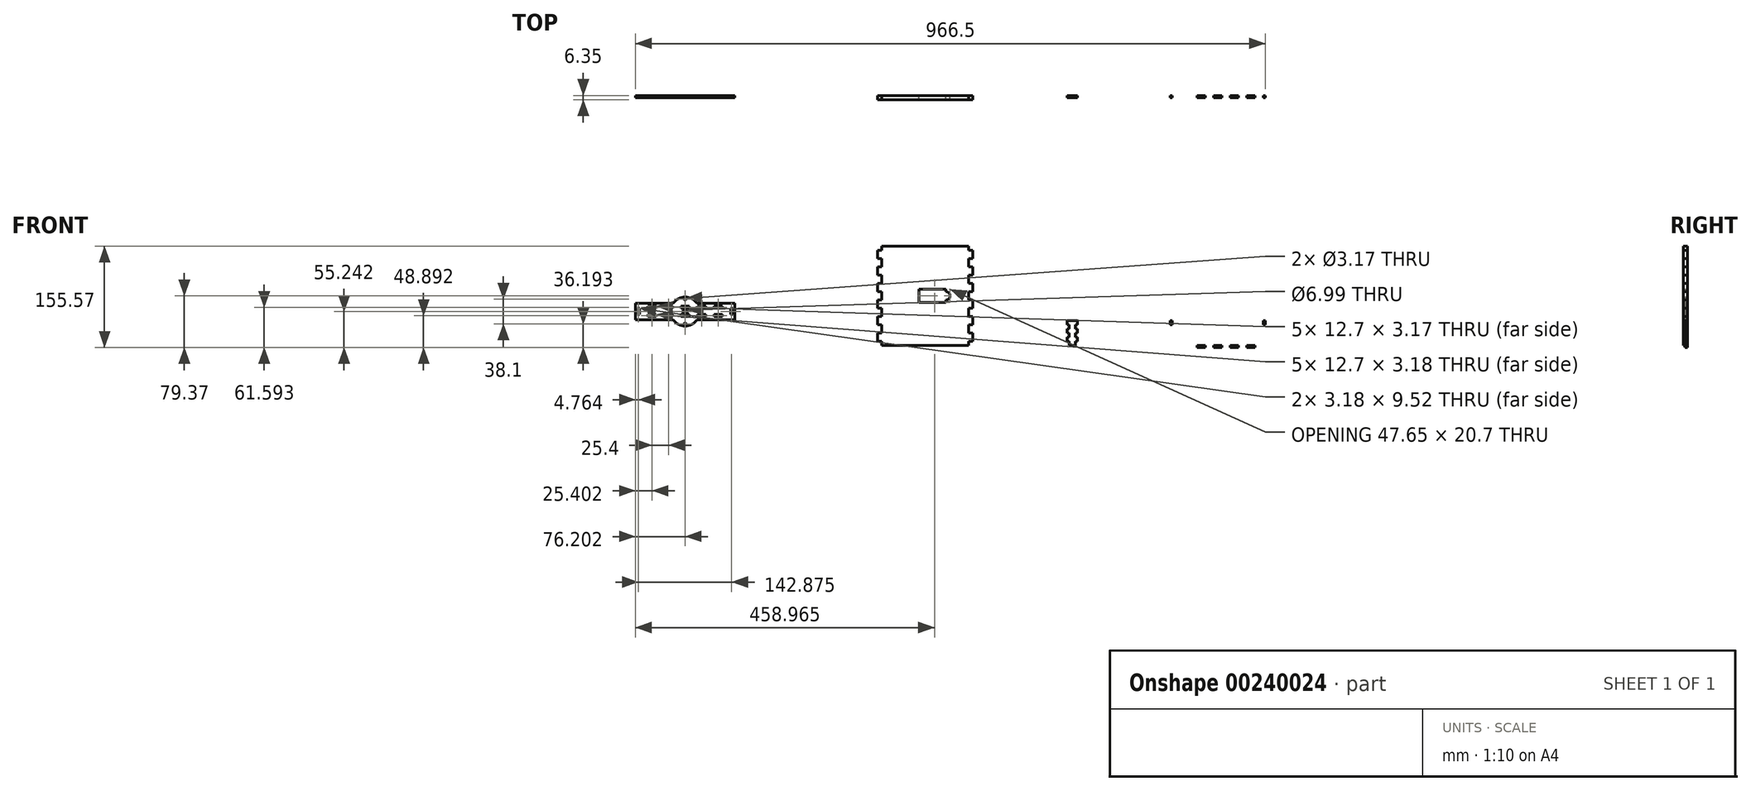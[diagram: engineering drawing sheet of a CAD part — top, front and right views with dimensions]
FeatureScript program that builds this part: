
annotation { "Feature Type Name" : "Feature", "Feature Type Description" : "" }
export const myFeature = defineFeature(function(context is Context, id is Id, definition is map)
    precondition{}
    {
        {
            var Q0;
            Q0=qCreatedBy(makeId("Front.planeOp"),FACE);
            var sketch = newSketch(context, id + "F0", { "sketchPlane" : qUnion([Q0])});
            skLineSegment(sketch, "E0.bottom", {"start": v(0, 0) * mm, "end": v(146.05, 0) * mm});
            skLineSegment(sketch, "E0.top", {"start": v(0, 38.1) * mm, "end": v(146.05, 38.1) * mm});
            skLineSegment(sketch, "E0.left", {"start": v(0, 0) * mm, "end": v(0, 38.1) * mm});
            skLineSegment(sketch, "E0.right", {"start": v(146.05, 0) * mm, "end": v(146.05, 38.1) * mm});
            skLineSegment(sketch, "E1.bottom", {"start": v(0, 38.1) * mm, "end": v(3.17, 38.1) * mm});
            skLineSegment(sketch, "E1.top", {"start": v(0, 31.75) * mm, "end": v(3.17, 31.75) * mm});
            skLineSegment(sketch, "E1.left", {"start": v(0, 38.1) * mm, "end": v(0, 31.75) * mm});
            skLineSegment(sketch, "E1.right", {"start": v(3.17, 38.1) * mm, "end": v(3.17, 31.75) * mm});
            skLineSegment(sketch, "E2.0.1.0", {"start": v(0, 19.05) * mm, "end": v(3.17, 19.05) * mm});
            skLineSegment(sketch, "E2.0.1.1", {"start": v(3.17, 25.4) * mm, "end": v(3.17, 19.05) * mm});
            skLineSegment(sketch, "E2.0.1.2", {"start": v(0, 25.4) * mm, "end": v(3.17, 25.4) * mm});
            skLineSegment(sketch, "E2.0.1.3", {"start": v(0, 25.4) * mm, "end": v(0, 19.05) * mm});
            skLineSegment(sketch, "E2.0.2.0", {"start": v(0, 6.35) * mm, "end": v(3.17, 6.35) * mm});
            skLineSegment(sketch, "E2.0.2.1", {"start": v(3.17, 12.7) * mm, "end": v(3.17, 6.35) * mm});
            skLineSegment(sketch, "E2.0.2.2", {"start": v(0, 12.7) * mm, "end": v(3.17, 12.7) * mm});
            skLineSegment(sketch, "E2.0.2.3", {"start": v(0, 12.7) * mm, "end": v(0, 6.35) * mm});
            skLineSegment(sketch, "E2.direction1", {"start": v(0, 25.4) * mm, "end": v(25.4, 25.4) * mm, "construction": true});
            skLineSegment(sketch, "E2.direction2", {"start": v(0, 25.4) * mm, "end": v(0, 12.7) * mm, "construction": true});
            skLineSegment(sketch, "E3.bottom", {"start": v(15.88, 0) * mm, "end": v(28.58, 0) * mm});
            skLineSegment(sketch, "E3.top", {"start": v(15.88, -3.18) * mm, "end": v(28.58, -3.18) * mm});
            skLineSegment(sketch, "E3.left", {"start": v(15.88, 0) * mm, "end": v(15.88, -3.18) * mm});
            skLineSegment(sketch, "E3.right", {"start": v(28.58, 0) * mm, "end": v(28.58, -3.18) * mm});
            skLineSegment(sketch, "E4.1.0.0", {"start": v(41.27, -3.18) * mm, "end": v(53.97, -3.18) * mm});
            skLineSegment(sketch, "E4.1.0.1", {"start": v(53.97, 0) * mm, "end": v(53.97, -3.18) * mm});
            skLineSegment(sketch, "E4.1.0.2", {"start": v(41.27, 0) * mm, "end": v(41.27, -3.18) * mm});
            skLineSegment(sketch, "E4.1.0.3", {"start": v(41.27, 0) * mm, "end": v(53.97, 0) * mm});
            skLineSegment(sketch, "E4.2.0.0", {"start": v(66.67, -3.18) * mm, "end": v(79.37, -3.18) * mm});
            skLineSegment(sketch, "E4.2.0.1", {"start": v(79.37, 0) * mm, "end": v(79.37, -3.18) * mm});
            skLineSegment(sketch, "E4.2.0.2", {"start": v(66.67, 0) * mm, "end": v(66.67, -3.18) * mm});
            skLineSegment(sketch, "E4.2.0.3", {"start": v(66.67, 0) * mm, "end": v(79.37, 0) * mm});
            skLineSegment(sketch, "E4.3.0.0", {"start": v(92.07, -3.18) * mm, "end": v(104.77, -3.18) * mm});
            skLineSegment(sketch, "E4.3.0.1", {"start": v(104.77, 0) * mm, "end": v(104.77, -3.18) * mm});
            skLineSegment(sketch, "E4.3.0.2", {"start": v(92.07, 0) * mm, "end": v(92.07, -3.18) * mm});
            skLineSegment(sketch, "E4.3.0.3", {"start": v(92.07, 0) * mm, "end": v(104.77, 0) * mm});
            skLineSegment(sketch, "E4.4.0.0", {"start": v(117.47, -3.18) * mm, "end": v(130.17, -3.18) * mm});
            skLineSegment(sketch, "E4.4.0.1", {"start": v(130.17, 0) * mm, "end": v(130.17, -3.18) * mm});
            skLineSegment(sketch, "E4.4.0.2", {"start": v(117.47, 0) * mm, "end": v(117.47, -3.18) * mm});
            skLineSegment(sketch, "E4.4.0.3", {"start": v(117.47, 0) * mm, "end": v(130.17, 0) * mm});
            skLineSegment(sketch, "E4.direction1", {"start": v(3.18, -3.18) * mm, "end": v(28.58, -3.18) * mm, "construction": true});
            skLineSegment(sketch, "E5", {"start": v(73.03, 38.1) * mm, "end": v(73.03, 0) * mm, "construction": true});
            skLineSegment(sketch, "E6.MirrorCS", {"start": v(146.05, 12.7) * mm, "end": v(142.88, 12.7) * mm});
            skLineSegment(sketch, "E7.MirrorCS", {"start": v(146.05, 31.75) * mm, "end": v(142.88, 31.75) * mm});
            skLineSegment(sketch, "E8.MirrorCS", {"start": v(146.05, 19.05) * mm, "end": v(142.88, 19.05) * mm});
            skLineSegment(sketch, "E9.MirrorCS", {"start": v(146.05, 25.4) * mm, "end": v(142.88, 25.4) * mm});
            skLineSegment(sketch, "E10.MirrorCS", {"start": v(146.05, 6.35) * mm, "end": v(142.88, 6.35) * mm});
            skLineSegment(sketch, "E11.MirrorCS", {"start": v(142.88, 12.7) * mm, "end": v(142.88, 6.35) * mm});
            skLineSegment(sketch, "E12.MirrorCS", {"start": v(142.88, 38.1) * mm, "end": v(142.88, 31.75) * mm});
            skLineSegment(sketch, "E13.MirrorCS", {"start": v(142.88, 25.4) * mm, "end": v(142.88, 19.05) * mm});
            skLineSegment(sketch, "E14.MirrorCS", {"start": v(146.05, 25.4) * mm, "end": v(120.65, 25.4) * mm, "construction": true});
            skLineSegment(sketch, "E15.MirrorCS", {"start": v(146.05, 38.1) * mm, "end": v(142.88, 38.1) * mm});
            skLineSegment(sketch, "E16.MirrorCS", {"start": v(146.05, 38.1) * mm, "end": v(146.05, 31.75) * mm});
            skLineSegment(sketch, "E17.MirrorCS", {"start": v(146.05, 25.4) * mm, "end": v(146.05, 12.7) * mm, "construction": true});
            skSolve(sketch);
        }
        {
            var Q0;
            Q0=makeQuery(id+"F0.imprint","IMPRINT",FACE,{"disambiguationData":[TD([[makeQuery(id+"F0.imprint","IMPRINT",EDGE,{"derivedFrom":sQuery(id+"F0.wireOp",EDGE,"E0.top")}),-1.0]])]});
            var Q1;
            Q1=makeQuery(id+"F0.imprint","IMPRINT",FACE,{"disambiguationData":[TD([[makeQuery(id+"F0.imprint","IMPRINT",EDGE,{"derivedFrom":sQuery(id+"F0.wireOp",EDGE,"E3.bottom")}),-1.0]])]});
            var Q2;
            Q2=makeQuery(id+"F0.imprint","IMPRINT",FACE,{"disambiguationData":[TD([[makeQuery(id+"F0.imprint","IMPRINT",EDGE,{"derivedFrom":sQuery(id+"F0.wireOp",EDGE,"E4.1.0.0")}),1.0]])]});
            var Q3;
            Q3=makeQuery(id+"F0.imprint","IMPRINT",FACE,{"disambiguationData":[TD([[makeQuery(id+"F0.imprint","IMPRINT",EDGE,{"derivedFrom":sQuery(id+"F0.wireOp",EDGE,"E4.2.0.0")}),1.0]])]});
            var Q4;
            Q4=makeQuery(id+"F0.imprint","IMPRINT",FACE,{"disambiguationData":[TD([[makeQuery(id+"F0.imprint","IMPRINT",EDGE,{"derivedFrom":sQuery(id+"F0.wireOp",EDGE,"E4.3.0.0")}),1.0]])]});
            var Q5;
            Q5=makeQuery(id+"F0.imprint","IMPRINT",FACE,{"disambiguationData":[TD([[makeQuery(id+"F0.imprint","IMPRINT",EDGE,{"derivedFrom":sQuery(id+"F0.wireOp",EDGE,"E4.4.0.0")}),1.0]])]});
            extrude(context, id + "F1", {"entities" : qUnion([Q0, Q1, Q2, Q3, Q4, Q5]), "depth" : 3.17 * mm});
        }
        {
            var Q0;
            Q0=qCreatedBy(makeId("Front.planeOp"),FACE);
            var sketch = newSketch(context, id + "F2", { "sketchPlane" : qUnion([Q0])});
            skLineSegment(sketch, "E18.bottom", {"start": v(-145.64, 0) * mm, "end": v(-155.16, 0) * mm});
            skLineSegment(sketch, "E18.top", {"start": v(-145.64, 38.1) * mm, "end": v(-155.16, 38.1) * mm});
            skLineSegment(sketch, "E18.left", {"start": v(-145.64, 0) * mm, "end": v(-145.64, 38.1) * mm});
            skLineSegment(sketch, "E18.right", {"start": v(-155.16, 0) * mm, "end": v(-155.16, 38.1) * mm});
            skLineSegment(sketch, "E19.bottom", {"start": v(-145.64, 38.1) * mm, "end": v(-142.46, 38.1) * mm});
            skLineSegment(sketch, "E19.top", {"start": v(-145.64, 31.75) * mm, "end": v(-142.46, 31.75) * mm});
            skLineSegment(sketch, "E19.left", {"start": v(-145.64, 38.1) * mm, "end": v(-145.64, 31.75) * mm});
            skLineSegment(sketch, "E19.right", {"start": v(-142.46, 38.1) * mm, "end": v(-142.46, 31.75) * mm});
            skLineSegment(sketch, "E20.0.1.0", {"start": v(-142.46, 25.4) * mm, "end": v(-142.46, 19.05) * mm});
            skLineSegment(sketch, "E20.0.1.1", {"start": v(-145.64, 25.4) * mm, "end": v(-142.46, 25.4) * mm});
            skLineSegment(sketch, "E20.0.1.2", {"start": v(-145.64, 19.05) * mm, "end": v(-142.46, 19.05) * mm});
            skLineSegment(sketch, "E20.0.1.3", {"start": v(-155.16, -12.7) * mm, "end": v(-155.16, 25.4) * mm});
            skLineSegment(sketch, "E20.0.2.0", {"start": v(-142.46, 12.7) * mm, "end": v(-142.46, 6.35) * mm});
            skLineSegment(sketch, "E20.0.2.1", {"start": v(-145.64, 12.7) * mm, "end": v(-142.46, 12.7) * mm});
            skLineSegment(sketch, "E20.0.2.2", {"start": v(-145.64, 6.35) * mm, "end": v(-142.46, 6.35) * mm});
            skLineSegment(sketch, "E20.0.2.3", {"start": v(-155.16, -25.4) * mm, "end": v(-155.16, 12.7) * mm});
            skLineSegment(sketch, "E20.direction1", {"start": v(-145.64, 31.75) * mm, "end": v(-122.14, 31.75) * mm, "construction": true});
            skLineSegment(sketch, "E20.direction2", {"start": v(-145.64, 31.75) * mm, "end": v(-145.64, 19.05) * mm, "construction": true});
            skLineSegment(sketch, "E21", {"start": v(-150.4, 38.1) * mm, "end": v(-150.4, 0) * mm, "construction": true});
            skLineSegment(sketch, "E22.MirrorCS", {"start": v(-155.16, 25.4) * mm, "end": v(-158.34, 25.4) * mm});
            skLineSegment(sketch, "E23.MirrorCS", {"start": v(-155.16, 19.05) * mm, "end": v(-158.34, 19.05) * mm});
            skLineSegment(sketch, "E24.MirrorCS", {"start": v(-155.16, 31.75) * mm, "end": v(-158.34, 31.75) * mm});
            skLineSegment(sketch, "E25.MirrorCS", {"start": v(-155.16, 38.1) * mm, "end": v(-158.34, 38.1) * mm});
            skLineSegment(sketch, "E26.MirrorCS", {"start": v(-155.16, 12.7) * mm, "end": v(-158.34, 12.7) * mm});
            skLineSegment(sketch, "E27.MirrorCS", {"start": v(-155.16, 6.35) * mm, "end": v(-158.34, 6.35) * mm});
            skLineSegment(sketch, "E28.MirrorCS", {"start": v(-158.34, 38.1) * mm, "end": v(-158.34, 31.75) * mm});
            skLineSegment(sketch, "E29.MirrorCS", {"start": v(-158.34, 25.4) * mm, "end": v(-158.34, 19.05) * mm});
            skLineSegment(sketch, "E30.MirrorCS", {"start": v(-158.34, 12.7) * mm, "end": v(-158.34, 6.35) * mm});
            skLineSegment(sketch, "E31.MirrorCS", {"start": v(-155.16, 31.75) * mm, "end": v(-178.66, 31.75) * mm, "construction": true});
            skLineSegment(sketch, "E32.bottom", {"start": v(-155.16, 0) * mm, "end": v(-145.64, 0) * mm});
            skLineSegment(sketch, "E32.top", {"start": v(-155.16, -3.18) * mm, "end": v(-145.64, -3.18) * mm});
            skLineSegment(sketch, "E32.left", {"start": v(-155.16, 0) * mm, "end": v(-155.16, -3.18) * mm});
            skLineSegment(sketch, "E32.right", {"start": v(-145.64, 0) * mm, "end": v(-145.64, -3.18) * mm});
            skSolve(sketch);
        }
        {
            var Q0;
            {var subQ7=sQuery(id+"F2.wireOp",EDGE,"E18.top");Q0=makeQuery(id+"F2.imprint","IMPRINT",FACE,{"disambiguationData":[TD([[makeQuery(id+"F2.imprint","IMPRINT",EDGE,{"derivedFrom":subQ7}),1.0]])]});}
            var Q1;
            {var subQ0=sQuery(id+"F2.wireOp",EDGE,"E22.MirrorCS");Q1=makeQuery(id+"F2.imprint","IMPRINT",FACE,{"disambiguationData":[TD([[makeQuery(id+"F2.imprint","IMPRINT",EDGE,{"derivedFrom":subQ0}),1.0]])]});}
            var Q2;
            {var subQ0=sQuery(id+"F2.wireOp",EDGE,"E26.MirrorCS");Q2=makeQuery(id+"F2.imprint","IMPRINT",FACE,{"disambiguationData":[TD([[makeQuery(id+"F2.imprint","IMPRINT",EDGE,{"derivedFrom":subQ0}),1.0]])]});}
            var Q3;
            Q3=makeQuery(id+"F2.imprint","IMPRINT",FACE,{"disambiguationData":[TD([[makeQuery(id+"F2.imprint","IMPRINT",EDGE,{"derivedFrom":sQuery(id+"F2.wireOp",EDGE,"E20.0.2.0")}),-1.0]])]});
            var Q4;
            Q4=makeQuery(id+"F2.imprint","IMPRINT",FACE,{"disambiguationData":[TD([[makeQuery(id+"F2.imprint","IMPRINT",EDGE,{"derivedFrom":sQuery(id+"F2.wireOp",EDGE,"E20.0.1.0")}),-1.0]])]});
            var Q5;
            Q5=makeQuery(id+"F2.imprint","IMPRINT",FACE,{"disambiguationData":[TD([[makeQuery(id+"F2.imprint","IMPRINT",EDGE,{"derivedFrom":sQuery(id+"F2.wireOp",EDGE,"E19.bottom")}),-1.0]])]});
            var Q6;
            {var subQ2=sQuery(id+"F2.wireOp",EDGE,"E24.MirrorCS");Q6=makeQuery(id+"F2.imprint","IMPRINT",FACE,{"disambiguationData":[TD([[makeQuery(id+"F2.imprint","IMPRINT",EDGE,{"derivedFrom":subQ2}),-1.0]])]});}
            var Q7;
            Q7=makeQuery(id+"F2.imprint","IMPRINT",FACE,{"disambiguationData":[TD([[makeQuery(id+"F2.imprint","IMPRINT",EDGE,{"derivedFrom":sQuery(id+"F2.wireOp",EDGE,"E32.bottom")}),-1.0]])]});
            extrude(context, id + "F3", {"entities" : qUnion([Q0, Q1, Q2, Q3, Q4, Q5, Q6, Q7]), "depth" : 3.17 * mm});
        }
        {
            var Q0;
            Q0=qCreatedBy(makeId("Front.planeOp"),FACE);
            var sketch = newSketch(context, id + "F4", { "sketchPlane" : qUnion([Q0])});
            skLineSegment(sketch, "E33.bottom", {"start": v(-309.1, 0) * mm, "end": v(-442.46, 0) * mm});
            skLineSegment(sketch, "E33.top", {"start": v(-309.1, 152.4) * mm, "end": v(-442.46, 152.4) * mm});
            skLineSegment(sketch, "E33.left", {"start": v(-309.1, 0) * mm, "end": v(-309.1, 152.4) * mm});
            skLineSegment(sketch, "E33.right", {"start": v(-442.46, 0) * mm, "end": v(-442.46, 152.4) * mm});
            skLineSegment(sketch, "E34.bottom", {"start": v(-309.1, 146.05) * mm, "end": v(-302.76, 146.05) * mm});
            skLineSegment(sketch, "E34.top", {"start": v(-309.1, 133.35) * mm, "end": v(-302.76, 133.35) * mm});
            skLineSegment(sketch, "E34.left", {"start": v(-309.1, 146.05) * mm, "end": v(-309.1, 133.35) * mm});
            skLineSegment(sketch, "E34.right", {"start": v(-302.76, 146.05) * mm, "end": v(-302.76, 133.35) * mm});
            skLineSegment(sketch, "E35.0.1.0", {"start": v(-309.1, 107.95) * mm, "end": v(-302.76, 107.95) * mm});
            skLineSegment(sketch, "E35.0.1.1", {"start": v(-309.1, 120.65) * mm, "end": v(-302.76, 120.65) * mm});
            skLineSegment(sketch, "E35.0.1.2", {"start": v(-302.76, 120.65) * mm, "end": v(-302.76, 107.95) * mm});
            skLineSegment(sketch, "E35.0.2.0", {"start": v(-309.1, 82.55) * mm, "end": v(-302.76, 82.55) * mm});
            skLineSegment(sketch, "E35.0.2.1", {"start": v(-309.1, 95.25) * mm, "end": v(-302.76, 95.25) * mm});
            skLineSegment(sketch, "E35.0.2.2", {"start": v(-302.76, 95.25) * mm, "end": v(-302.76, 82.55) * mm});
            skLineSegment(sketch, "E35.0.3.0", {"start": v(-309.1, 57.15) * mm, "end": v(-302.76, 57.15) * mm});
            skLineSegment(sketch, "E35.0.3.1", {"start": v(-309.1, 69.85) * mm, "end": v(-302.76, 69.85) * mm});
            skLineSegment(sketch, "E35.0.3.2", {"start": v(-302.76, 69.85) * mm, "end": v(-302.76, 57.15) * mm});
            skLineSegment(sketch, "E35.0.4.0", {"start": v(-309.1, 31.75) * mm, "end": v(-302.76, 31.75) * mm});
            skLineSegment(sketch, "E35.0.4.1", {"start": v(-309.1, 44.45) * mm, "end": v(-302.76, 44.45) * mm});
            skLineSegment(sketch, "E35.0.4.2", {"start": v(-302.76, 44.45) * mm, "end": v(-302.76, 31.75) * mm});
            skLineSegment(sketch, "E35.0.5.0", {"start": v(-309.1, 6.35) * mm, "end": v(-302.76, 6.35) * mm});
            skLineSegment(sketch, "E35.0.5.1", {"start": v(-309.1, 19.05) * mm, "end": v(-302.76, 19.05) * mm});
            skLineSegment(sketch, "E35.0.5.2", {"start": v(-302.76, 19.05) * mm, "end": v(-302.76, 6.35) * mm});
            skLineSegment(sketch, "E35.direction1", {"start": v(-309.1, 133.35) * mm, "end": v(-283.7, 133.35) * mm, "construction": true});
            skLineSegment(sketch, "E35.direction2", {"start": v(-309.1, 133.35) * mm, "end": v(-309.1, 107.95) * mm, "construction": true});
            skLineSegment(sketch, "E36", {"start": v(-375.78, 152.4) * mm, "end": v(-375.78, 0) * mm, "construction": true});
            skLineSegment(sketch, "E37.MirrorCS", {"start": v(-442.46, 31.75) * mm, "end": v(-448.8, 31.75) * mm});
            skLineSegment(sketch, "E38.MirrorCS", {"start": v(-442.46, 57.15) * mm, "end": v(-448.8, 57.15) * mm});
            skLineSegment(sketch, "E39.MirrorCS", {"start": v(-442.46, 69.85) * mm, "end": v(-448.8, 69.85) * mm});
            skLineSegment(sketch, "E40.MirrorCS", {"start": v(-442.46, 146.05) * mm, "end": v(-448.8, 146.05) * mm});
            skLineSegment(sketch, "E41.MirrorCS", {"start": v(-442.46, 133.35) * mm, "end": v(-448.8, 133.35) * mm});
            skLineSegment(sketch, "E42.MirrorCS", {"start": v(-442.46, 107.95) * mm, "end": v(-448.8, 107.95) * mm});
            skLineSegment(sketch, "E43.MirrorCS", {"start": v(-442.46, 120.65) * mm, "end": v(-448.8, 120.65) * mm});
            skLineSegment(sketch, "E44.MirrorCS", {"start": v(-442.46, 6.35) * mm, "end": v(-448.8, 6.35) * mm});
            skLineSegment(sketch, "E45.MirrorCS", {"start": v(-442.46, 19.05) * mm, "end": v(-448.8, 19.05) * mm});
            skLineSegment(sketch, "E46.MirrorCS", {"start": v(-442.46, 82.55) * mm, "end": v(-448.8, 82.55) * mm});
            skLineSegment(sketch, "E47.MirrorCS", {"start": v(-442.46, 44.45) * mm, "end": v(-448.8, 44.45) * mm});
            skLineSegment(sketch, "E48.MirrorCS", {"start": v(-442.46, 95.25) * mm, "end": v(-448.8, 95.25) * mm});
            skLineSegment(sketch, "E49.MirrorCS", {"start": v(-448.8, 95.25) * mm, "end": v(-448.8, 82.55) * mm});
            skLineSegment(sketch, "E50.MirrorCS", {"start": v(-448.8, 69.85) * mm, "end": v(-448.8, 57.15) * mm});
            skLineSegment(sketch, "E51.MirrorCS", {"start": v(-442.46, 133.35) * mm, "end": v(-467.86, 133.35) * mm, "construction": true});
            skLineSegment(sketch, "E52.MirrorCS", {"start": v(-448.8, 146.05) * mm, "end": v(-448.8, 133.35) * mm});
            skLineSegment(sketch, "E53.MirrorCS", {"start": v(-448.8, 19.05) * mm, "end": v(-448.8, 6.35) * mm});
            skLineSegment(sketch, "E54.MirrorCS", {"start": v(-448.8, 120.65) * mm, "end": v(-448.8, 107.95) * mm});
            skLineSegment(sketch, "E55.MirrorCS", {"start": v(-448.8, 44.45) * mm, "end": v(-448.8, 31.75) * mm});
            skLineSegment(sketch, "E56.0.1.4", {"start": v(-442.46, -25.4) * mm, "end": v(-442.46, 127) * mm});
            skLineSegment(sketch, "E56.0.2.4", {"start": v(-442.46, -50.8) * mm, "end": v(-442.46, 101.6) * mm});
            skLineSegment(sketch, "E56.0.3.4", {"start": v(-442.46, -76.2) * mm, "end": v(-442.46, 76.2) * mm});
            skLineSegment(sketch, "E56.0.4.4", {"start": v(-442.46, -101.6) * mm, "end": v(-442.46, 50.8) * mm});
            skLineSegment(sketch, "E57", {"start": v(-421.82, 152.4) * mm, "end": v(-421.82, 0) * mm, "construction": true});
            skLineSegment(sketch, "E58.MirrorCS", {"start": v(-329.75, 152.4) * mm, "end": v(-329.75, 0) * mm, "construction": true});
            skLineSegment(sketch, "E59", {"start": v(-309.1, 76.2) * mm, "end": v(-479.2, 76.2) * mm, "construction": true});
            skLineSegment(sketch, "E60.MirrorCS", {"start": v(-329.75, 0) * mm, "end": v(-329.75, 152.4) * mm, "construction": true});
            skLineSegment(sketch, "E61.MirrorCS", {"start": v(-421.82, 0) * mm, "end": v(-421.82, 152.4) * mm, "construction": true});
            skLineSegment(sketch, "E62.bottom", {"start": v(-385.3, 86.55) * mm, "end": v(-344, 86.55) * mm});
            skLineSegment(sketch, "E62.top", {"start": v(-385.3, 65.85) * mm, "end": v(-344, 65.85) * mm});
            skLineSegment(sketch, "E62.left", {"start": v(-385.3, 86.55) * mm, "end": v(-385.3, 65.85) * mm});
            skLineSegment(sketch, "E62.right", {"start": v(-344, 86.55) * mm, "end": v(-344, 65.85) * mm});
            skPoint(sketch, "E62.middle", {"position": v(-364.66, 76.2) * mm});
            skCircle(sketch, "E63", {"center": v(-344, 76.2) * mm, "radius": 6.35 * mm});
            skSolve(sketch);
        }
        {
            var Q0;
            Q0=qSketchRegion(id+"F4",true);
            extrude(context, id + "F5", {"entities" : qUnion([Q0]), "depth" : 6.35 * mm});
        }
        {
            var Q0;
            Q0=qCreatedBy(makeId("Front.planeOp"),FACE);
            var sketch = newSketch(context, id + "F6", { "sketchPlane" : qUnion([Q0])});
            skCircle(sketch, "E64", {"center": v(-744.25, 52.07) * mm, "radius": 22.23 * mm});
            skLineSegment(sketch, "E65.bottom", {"start": v(-668.05, 64.77) * mm, "end": v(-820.45, 64.77) * mm});
            skLineSegment(sketch, "E65.top", {"start": v(-668.05, 39.37) * mm, "end": v(-820.45, 39.37) * mm});
            skLineSegment(sketch, "E65.left", {"start": v(-668.05, 64.77) * mm, "end": v(-668.05, 39.37) * mm});
            skLineSegment(sketch, "E65.right", {"start": v(-820.45, 64.77) * mm, "end": v(-820.45, 39.37) * mm});
            skLineSegment(sketch, "E66", {"start": v(-744.25, 52.07) * mm, "end": v(-744.25, 74.3) * mm, "construction": true});
            skPoint(sketch, "E66.endSnap0", {"position": v(-744.25, 64.77) * mm});
            skCircle(sketch, "E67", {"center": v(-744.25, 71.12) * mm, "radius": 1.59 * mm});
            skLineSegment(sketch, "E68", {"start": v(-744.25, 52.07) * mm, "end": v(-722.02, 52.07) * mm, "construction": true});
            skCircle(sketch, "E69.MirrorC", {"center": v(-744.25, 33.02) * mm, "radius": 1.59 * mm});
            skCircle(sketch, "E70", {"center": v(-744.25, 52.07) * mm, "radius": 3.5 * mm});
            skSolve(sketch);
        }
        {
            var Q0;
            Q0=makeQuery(id+"F6.imprint","IMPRINT",FACE,{"disambiguationData":[TD([[makeQuery(id+"F6.imprint","IMPRINT",EDGE,{"derivedFrom":sQuery(id+"F6.wireOp",EDGE,"E64")}),1.0]])]});
            var Q1;
            {var subQ5=sQuery(id+"F6.wireOp",EDGE,"E65.right");Q1=makeQuery(id+"F6.imprint","IMPRINT",FACE,{"disambiguationData":[TD([[makeQuery(id+"F6.imprint","IMPRINT",EDGE,{"derivedFrom":subQ5}),1.0]])]});}
            var Q2;
            {var subQ5=sQuery(id+"F6.wireOp",EDGE,"E65.left");Q2=makeQuery(id+"F6.imprint","IMPRINT",FACE,{"disambiguationData":[TD([[makeQuery(id+"F6.imprint","IMPRINT",EDGE,{"derivedFrom":subQ5}),-1.0]])]});}
            var Q3;
            {var subQ0=sQuery(id+"F6.wireOp",EDGE,"E65.bottom");var subQ1=sQuery(id+"F6.wireOp",EDGE,"E64");var subQ2=makeQuery(id+"F6.imprint","INTERSECT",VERTEX,{"disambiguationData":[OD(0.0)],"derivedFrom":[subQ1,subQ0]});Q3=makeQuery(id+"F6.imprint","IMPRINT",FACE,{"disambiguationData":[TD([[makeQuery(id+"F6.imprint","IMPRINT",EDGE,{"disambiguationData":[TD([[subQ2,1.0]])],"derivedFrom":subQ1}),1.0]])]});}
            var Q4;
            {var subQ0=sQuery(id+"F6.wireOp",EDGE,"E65.top");var subQ1=sQuery(id+"F6.wireOp",EDGE,"E64");var subQ2=makeQuery(id+"F6.imprint","INTERSECT",VERTEX,{"disambiguationData":[OD(0.0)],"derivedFrom":[subQ1,subQ0]});Q4=makeQuery(id+"F6.imprint","IMPRINT",FACE,{"disambiguationData":[TD([[makeQuery(id+"F6.imprint","IMPRINT",EDGE,{"disambiguationData":[TD([[subQ2,-1.0]])],"derivedFrom":subQ1}),1.0]])]});}
            extrude(context, id + "F7", {"entities" : qUnion([Q0, Q1, Q2, Q3, Q4]), "depth" : 3.17 * mm});
        }
        {
            var Q0;
            Q0=makeQuery(id+"F7.opExtrude","CAP_FACE",FACE,{"disambiguationData":[OSD([sQuery(id+"F6.wireOp",EDGE,"E64"),sQuery(id+"F6.wireOp",EDGE,"E65.bottom"),sQuery(id+"F6.wireOp",EDGE,"E65.top"),sQuery(id+"F6.wireOp",EDGE,"E65.left"),sQuery(id+"F6.wireOp",EDGE,"E65.right"),sQuery(id+"F6.wireOp",EDGE,"E67"),sQuery(id+"F6.wireOp",EDGE,"E69.MirrorC")])],"isStart":false});
            var sketch = newSketch(context, id + "F8", { "sketchPlane" : qUnion([Q0])});
            skLineSegment(sketch, "E71.bottom", {"start": v(-750.6, 56.83) * mm, "end": v(-737.9, 56.83) * mm});
            skLineSegment(sketch, "E71.top", {"start": v(-750.6, 60) * mm, "end": v(-737.9, 60) * mm});
            skLineSegment(sketch, "E71.left", {"start": v(-750.6, 56.83) * mm, "end": v(-750.6, 60) * mm});
            skLineSegment(sketch, "E71.right", {"start": v(-737.9, 56.83) * mm, "end": v(-737.9, 60) * mm});
            skLineSegment(sketch, "E72", {"start": v(-820.45, 52.07) * mm, "end": v(-668.05, 52.07) * mm, "construction": true});
            skLineSegment(sketch, "E73", {"start": v(-744.25, 74.3) * mm, "end": v(-744.25, 29.85) * mm, "construction": true});
            skLineSegment(sketch, "E74.0.1.0", {"start": v(-763.3, 56.83) * mm, "end": v(-763.3, 60) * mm});
            skLineSegment(sketch, "E74.0.1.1", {"start": v(-776, 60) * mm, "end": v(-763.3, 60) * mm});
            skLineSegment(sketch, "E74.0.1.2", {"start": v(-776, 56.83) * mm, "end": v(-763.3, 56.83) * mm});
            skLineSegment(sketch, "E74.0.1.3", {"start": v(-769.65, 74.3) * mm, "end": v(-769.65, 29.85) * mm, "construction": true});
            skLineSegment(sketch, "E74.0.1.4", {"start": v(-776, 56.83) * mm, "end": v(-776, 60) * mm});
            skLineSegment(sketch, "E74.0.2.0", {"start": v(-788.7, 56.83) * mm, "end": v(-788.7, 60) * mm});
            skLineSegment(sketch, "E74.0.2.1", {"start": v(-801.4, 60) * mm, "end": v(-788.7, 60) * mm});
            skLineSegment(sketch, "E74.0.2.2", {"start": v(-801.4, 56.83) * mm, "end": v(-788.7, 56.83) * mm});
            skLineSegment(sketch, "E74.0.2.3", {"start": v(-795.05, 74.3) * mm, "end": v(-795.05, 29.85) * mm, "construction": true});
            skLineSegment(sketch, "E74.0.2.4", {"start": v(-801.4, 56.83) * mm, "end": v(-801.4, 60) * mm});
            skLineSegment(sketch, "E74.1.0.0", {"start": v(-712.5, 56.83) * mm, "end": v(-712.5, 60) * mm});
            skLineSegment(sketch, "E74.1.0.1", {"start": v(-725.2, 60) * mm, "end": v(-712.5, 60) * mm});
            skLineSegment(sketch, "E74.1.0.2", {"start": v(-725.2, 56.83) * mm, "end": v(-712.5, 56.83) * mm});
            skLineSegment(sketch, "E74.1.0.3", {"start": v(-718.85, 74.3) * mm, "end": v(-718.85, 29.85) * mm, "construction": true});
            skLineSegment(sketch, "E74.1.0.4", {"start": v(-725.2, 56.83) * mm, "end": v(-725.2, 60) * mm});
            skLineSegment(sketch, "E74.1.2.0", {"start": v(-763.3, 56.83) * mm, "end": v(-763.3, 60) * mm});
            skLineSegment(sketch, "E74.1.2.1", {"start": v(-776, 60) * mm, "end": v(-763.3, 60) * mm});
            skLineSegment(sketch, "E74.1.2.2", {"start": v(-776, 56.83) * mm, "end": v(-763.3, 56.83) * mm});
            skLineSegment(sketch, "E74.1.2.3", {"start": v(-769.65, 74.3) * mm, "end": v(-769.65, 29.85) * mm, "construction": true});
            skLineSegment(sketch, "E74.1.2.4", {"start": v(-776, 56.83) * mm, "end": v(-776, 60) * mm});
            skLineSegment(sketch, "E74.2.0.0", {"start": v(-687.1, 56.83) * mm, "end": v(-687.1, 60) * mm});
            skLineSegment(sketch, "E74.2.0.1", {"start": v(-699.8, 60) * mm, "end": v(-687.1, 60) * mm});
            skLineSegment(sketch, "E74.2.0.2", {"start": v(-699.8, 56.83) * mm, "end": v(-687.1, 56.83) * mm});
            skLineSegment(sketch, "E74.2.0.3", {"start": v(-693.45, 74.3) * mm, "end": v(-693.45, 29.85) * mm, "construction": true});
            skLineSegment(sketch, "E74.2.0.4", {"start": v(-699.8, 56.83) * mm, "end": v(-699.8, 60) * mm});
            skLineSegment(sketch, "E74.2.1.0", {"start": v(-712.5, 56.83) * mm, "end": v(-712.5, 60) * mm});
            skLineSegment(sketch, "E74.2.1.1", {"start": v(-725.2, 60) * mm, "end": v(-712.5, 60) * mm});
            skLineSegment(sketch, "E74.2.1.2", {"start": v(-725.2, 56.83) * mm, "end": v(-712.5, 56.83) * mm});
            skLineSegment(sketch, "E74.2.1.3", {"start": v(-718.85, 74.3) * mm, "end": v(-718.85, 29.85) * mm, "construction": true});
            skLineSegment(sketch, "E74.2.1.4", {"start": v(-725.2, 56.83) * mm, "end": v(-725.2, 60) * mm});
            skLineSegment(sketch, "E74.direction1", {"start": v(-744.25, 29.85) * mm, "end": v(-718.85, 29.85) * mm, "construction": true});
            skLineSegment(sketch, "E74.direction2", {"start": v(-744.25, 29.85) * mm, "end": v(-769.65, 29.85) * mm, "construction": true});
            skLineSegment(sketch, "E75.MirrorCS", {"start": v(-737.9, 47.3) * mm, "end": v(-737.9, 44.13) * mm});
            skLineSegment(sketch, "E76.MirrorCS", {"start": v(-750.6, 47.3) * mm, "end": v(-750.6, 44.13) * mm});
            skLineSegment(sketch, "E77.MirrorCS", {"start": v(-763.3, 47.3) * mm, "end": v(-763.3, 44.13) * mm});
            skLineSegment(sketch, "E78.MirrorCS", {"start": v(-776, 47.3) * mm, "end": v(-776, 44.13) * mm});
            skLineSegment(sketch, "E79.MirrorCS", {"start": v(-744.25, 29.85) * mm, "end": v(-744.25, 74.3) * mm, "construction": true});
            skLineSegment(sketch, "E80.MirrorCS", {"start": v(-712.5, 47.3) * mm, "end": v(-712.5, 44.13) * mm});
            skLineSegment(sketch, "E81.MirrorCS", {"start": v(-750.6, 44.13) * mm, "end": v(-737.9, 44.13) * mm});
            skLineSegment(sketch, "E82.MirrorCS", {"start": v(-725.2, 47.3) * mm, "end": v(-712.5, 47.3) * mm});
            skLineSegment(sketch, "E83.MirrorCS", {"start": v(-725.2, 47.3) * mm, "end": v(-725.2, 44.13) * mm});
            skLineSegment(sketch, "E84.MirrorCS", {"start": v(-725.2, 44.13) * mm, "end": v(-712.5, 44.13) * mm});
            skLineSegment(sketch, "E85.MirrorCS", {"start": v(-718.85, 29.85) * mm, "end": v(-718.85, 74.3) * mm, "construction": true});
            skLineSegment(sketch, "E86.MirrorCS", {"start": v(-769.65, 29.85) * mm, "end": v(-769.65, 74.3) * mm, "construction": true});
            skLineSegment(sketch, "E87.MirrorCS", {"start": v(-750.6, 47.3) * mm, "end": v(-737.9, 47.3) * mm});
            skLineSegment(sketch, "E88.MirrorCS", {"start": v(-795.05, 29.85) * mm, "end": v(-795.05, 74.3) * mm, "construction": true});
            skLineSegment(sketch, "E89.MirrorCS", {"start": v(-801.4, 47.3) * mm, "end": v(-801.4, 44.13) * mm});
            skLineSegment(sketch, "E90.MirrorCS", {"start": v(-776, 44.13) * mm, "end": v(-763.3, 44.13) * mm});
            skLineSegment(sketch, "E91.MirrorCS", {"start": v(-801.4, 47.3) * mm, "end": v(-788.7, 47.3) * mm});
            skLineSegment(sketch, "E92.MirrorCS", {"start": v(-699.8, 44.13) * mm, "end": v(-687.1, 44.13) * mm});
            skLineSegment(sketch, "E93.MirrorCS", {"start": v(-699.8, 47.3) * mm, "end": v(-699.8, 44.13) * mm});
            skLineSegment(sketch, "E94.MirrorCS", {"start": v(-687.1, 47.3) * mm, "end": v(-687.1, 44.13) * mm});
            skLineSegment(sketch, "E95.MirrorCS", {"start": v(-693.45, 29.85) * mm, "end": v(-693.45, 74.3) * mm, "construction": true});
            skLineSegment(sketch, "E96.MirrorCS", {"start": v(-699.8, 47.3) * mm, "end": v(-687.1, 47.3) * mm});
            skLineSegment(sketch, "E97.MirrorCS", {"start": v(-776, 47.3) * mm, "end": v(-763.3, 47.3) * mm});
            skLineSegment(sketch, "E98.MirrorCS", {"start": v(-801.4, 44.13) * mm, "end": v(-788.7, 44.13) * mm});
            skLineSegment(sketch, "E99.MirrorCS", {"start": v(-788.7, 47.3) * mm, "end": v(-788.7, 44.13) * mm});
            skLineSegment(sketch, "E100.bottom", {"start": v(-814.1, 56.83) * mm, "end": v(-817.27, 56.83) * mm});
            skLineSegment(sketch, "E100.top", {"start": v(-814.1, 47.3) * mm, "end": v(-817.27, 47.3) * mm});
            skLineSegment(sketch, "E100.left", {"start": v(-814.1, 56.83) * mm, "end": v(-814.1, 47.3) * mm});
            skLineSegment(sketch, "E100.right", {"start": v(-817.27, 56.83) * mm, "end": v(-817.27, 47.3) * mm});
            skPoint(sketch, "E100.middle", {"position": v(-815.69, 52.07) * mm});
            skPoint(sketch, "E101.MirrorP", {"position": v(-672.81, 52.07) * mm});
            skLineSegment(sketch, "E102.MirrorCS", {"start": v(-674.4, 56.83) * mm, "end": v(-674.4, 47.3) * mm});
            skLineSegment(sketch, "E103.MirrorCS", {"start": v(-674.4, 56.83) * mm, "end": v(-671.22, 56.83) * mm});
            skLineSegment(sketch, "E104.MirrorCS", {"start": v(-674.4, 47.3) * mm, "end": v(-671.22, 47.3) * mm});
            skLineSegment(sketch, "E105.MirrorCS", {"start": v(-668.05, 52.07) * mm, "end": v(-820.45, 52.07) * mm, "construction": true});
            skLineSegment(sketch, "E106.MirrorCS", {"start": v(-671.22, 56.83) * mm, "end": v(-671.22, 47.3) * mm});
            skSolve(sketch);
        }
        {
            var Q0;
            Q0 = qSketchRegion(id + "F8", true);
            extrude(context, id + "F9", {"entities" : qUnion([Q0]), "operationType" : NewBodyOperationType.REMOVE, "endBound" : BoundingType.UP_TO_NEXT, "oppositeDirection" : true, "depth" : 25.4 * mm});
        }
    });
